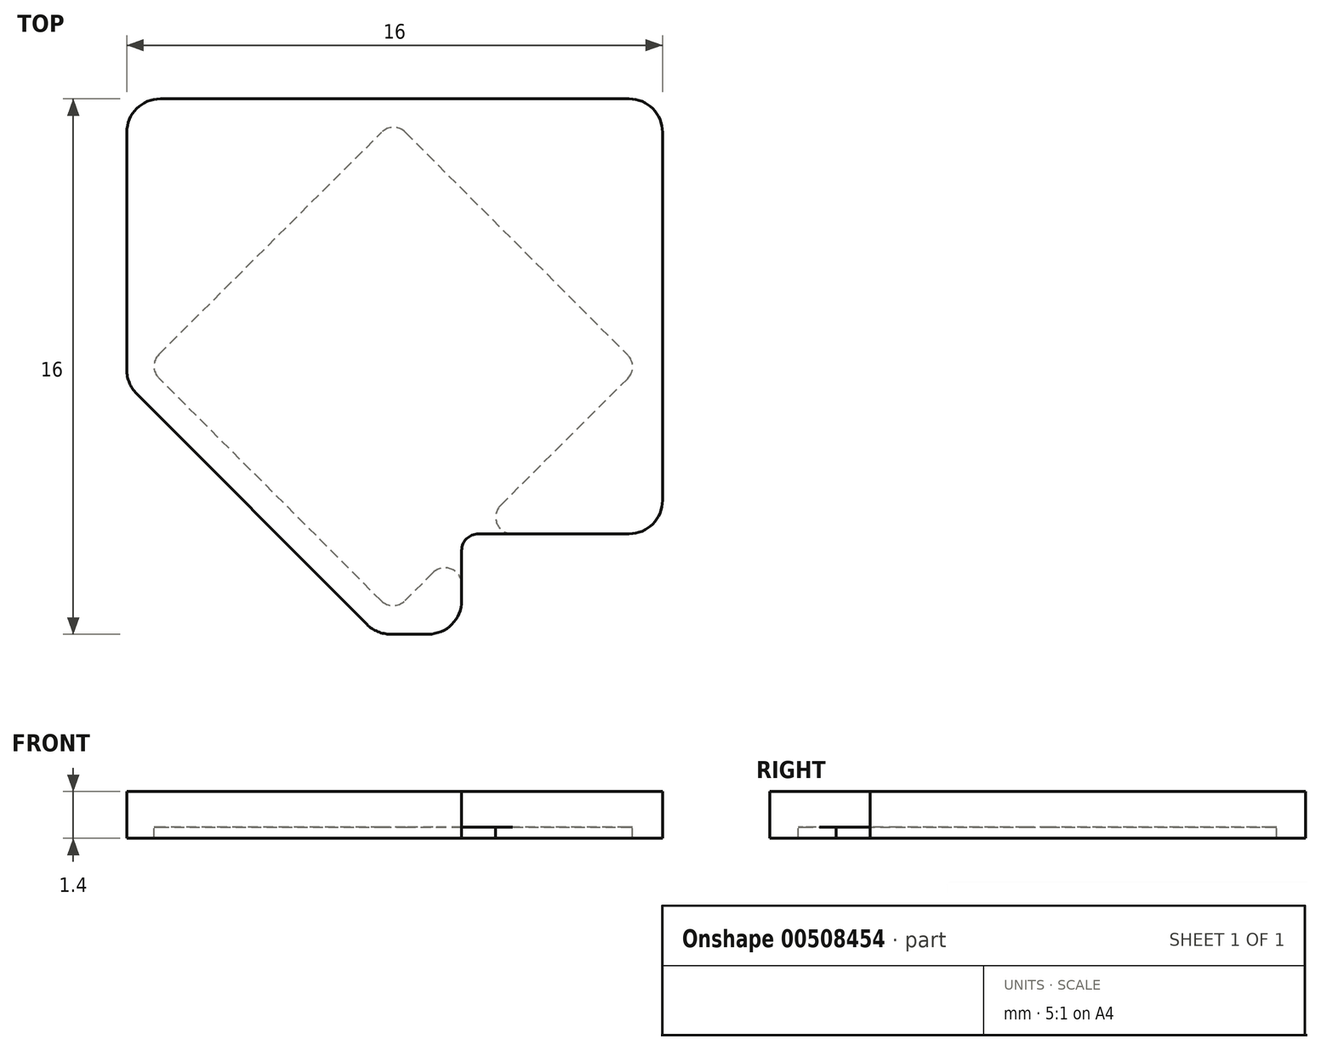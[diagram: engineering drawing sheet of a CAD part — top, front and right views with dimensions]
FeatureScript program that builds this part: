
annotation { "Feature Type Name" : "Feature", "Feature Type Description" : "" }
export const myFeature = defineFeature(function(context is Context, id is Id, definition is map)
    precondition{}
    {
        {
            var Q0;
            Q0=qCreatedBy(makeId("Top.planeOp"),FACE);
            var sketch = newSketch(context, id + "F0", { "sketchPlane" : qUnion([Q0])});
            skLineSegment(sketch, "E0.bottom", {"start": v(0, 0) * mm, "end": v(16, 0) * mm});
            skLineSegment(sketch, "E0.top", {"start": v(0, 16) * mm, "end": v(16, 16) * mm});
            skLineSegment(sketch, "E0.left", {"start": v(0, 0) * mm, "end": v(0, 16) * mm});
            skLineSegment(sketch, "E0.right", {"start": v(16, 0) * mm, "end": v(16, 16) * mm});
            skPoint(sketch, "E1.cCircle.centerSnap0", {"position": v(16, 8) * mm});
            skCircle(sketch, "E2.cCircle", {"center": v(7.96, 8) * mm, "radius": 5.2 * mm, "construction": true});
            skLineSegment(sketch, "E2.0", {"start": v(15.31, 8) * mm, "end": v(7.95, 0.65) * mm});
            skLineSegment(sketch, "E2.1", {"start": v(7.95, 0.65) * mm, "end": v(0.6, 8) * mm});
            skLineSegment(sketch, "E2.2", {"start": v(0.6, 8) * mm, "end": v(7.97, 15.35) * mm});
            skLineSegment(sketch, "E2.3", {"start": v(7.97, 15.35) * mm, "end": v(15.31, 8) * mm});
            skPoint(sketch, "E2.0.midPoint", {"position": v(11.63, 4.32) * mm});
            skLineSegment(sketch, "E3.bottom", {"start": v(16, 3) * mm, "end": v(10, 3) * mm});
            skLineSegment(sketch, "E3.top", {"start": v(16, 0) * mm, "end": v(10, 0) * mm});
            skLineSegment(sketch, "E3.left", {"start": v(16, 3) * mm, "end": v(16, 0) * mm});
            skLineSegment(sketch, "E3.right", {"start": v(10, 3) * mm, "end": v(10, 0) * mm});
            skLineSegment(sketch, "E4", {"start": v(2.16, 5.32) * mm, "end": v(5.62, 1.85) * mm});
            skLineSegment(sketch, "E5", {"start": v(2.16, 5.32) * mm, "end": v(0, 7.48) * mm});
            skLineSegment(sketch, "E6", {"start": v(5.62, 1.85) * mm, "end": v(7.46, 0) * mm});
            skSolve(sketch);
        }
        {
            var Q0;
            {var subQ11=sQuery(id+"F0.wireOp",EDGE,"E0.top");Q0=makeQuery(id+"F0.imprint","IMPRINT",FACE,{"disambiguationData":[TD([[makeQuery(id+"F0.imprint","IMPRINT",EDGE,{"derivedFrom":subQ11}),-1.0]])]});}
            extrude(context, id + "F1", {"entities" : qUnion([Q0]), "depth" : 1.4 * mm, "offsetDistance" : 25 * mm});
        }
        {
            var Q0;
            Q0=makeQuery(id+"F0.imprint","IMPRINT",FACE,{"disambiguationData":[TD([[makeQuery(id+"F0.imprint","IMPRINT",EDGE,{"derivedFrom":sQuery(id+"F0.wireOp",EDGE,"E2.0")}),-1.0]])]});
            extrude(context, id + "F2", {"entities" : qUnion([Q0]), "operationType" : NewBodyOperationType.ADD, "depth" : 1.4 * mm, "offsetDistance" : 25 * mm, "hasSecondDirection" : true, "secondDirectionOppositeDirection" : false, "secondDirectionDepth" : 0.33 * mm});
        }
        {
            var Q0;
            Q0=makeQuery(id+"F1.opExtrude","SWEPT_EDGE",EDGE,{"disambiguationData":[OSD([sQuery(id+"F0.wireOp",EDGE,"E0.bottom"),sQuery(id+"F0.wireOp",EDGE,"E0.left")])]});
            var Q1;
            Q1=makeQuery(id+"F1.opExtrude","SWEPT_EDGE",EDGE,{"disambiguationData":[OSD([sQuery(id+"F0.wireOp",EDGE,"E0.bottom"),sQuery(id+"F0.wireOp",EDGE,"E0.right")])]});
            var Q2;
            Q2=makeQuery(id+"F1.opExtrude","SWEPT_EDGE",EDGE,{"disambiguationData":[OSD([sQuery(id+"F0.wireOp",EDGE,"E0.top"),sQuery(id+"F0.wireOp",EDGE,"E0.right")])]});
            var Q3;
            Q3=makeQuery(id+"F1.opExtrude","SWEPT_EDGE",EDGE,{"disambiguationData":[OSD([sQuery(id+"F0.wireOp",EDGE,"E0.top"),sQuery(id+"F0.wireOp",EDGE,"E0.left")])]});
            var Q4;
            Q4=makeQuery(id+"F1.opExtrude","SWEPT_EDGE",EDGE,{"disambiguationData":[OSD([sQuery(id+"F0.wireOp",EDGE,"E0.bottom"),sQuery(id+"F0.wireOp",EDGE,"E3.top"),sQuery(id+"F0.wireOp",EDGE,"E3.right")])]});
            var Q5;
            Q5=makeQuery(id+"F1.opExtrude","SWEPT_EDGE",EDGE,{"disambiguationData":[OSD([sQuery(id+"F0.wireOp",EDGE,"E0.right"),sQuery(id+"F0.wireOp",EDGE,"E3.bottom"),sQuery(id+"F0.wireOp",EDGE,"E3.left")])]});
            fillet(context, id + "F3", {"entities" : qUnion([Q0, Q1, Q2, Q3, Q4, Q5]), "radius" : 1 * mm, "tangentPropagation" : true, "allowEdgeOverflow" : false});
        }
        {
            var Q0;
            Q0=makeQuery(id+"F1.opExtrude","SWEPT_EDGE",EDGE,{"disambiguationData":[OSD([sQuery(id+"F0.wireOp",EDGE,"E2.2"),sQuery(id+"F0.wireOp",EDGE,"E2.3")])]});
            var Q1;
            Q1=makeQuery(id+"F1.opExtrude","SWEPT_EDGE",EDGE,{"disambiguationData":[OSD([sQuery(id+"F0.wireOp",EDGE,"E2.1"),sQuery(id+"F0.wireOp",EDGE,"E2.2")])]});
            var Q2;
            Q2=makeQuery(id+"F1.opExtrude","SWEPT_EDGE",EDGE,{"disambiguationData":[OSD([sQuery(id+"F0.wireOp",EDGE,"E2.0"),sQuery(id+"F0.wireOp",EDGE,"E2.1")])]});
            var Q3;
            Q3=makeQuery(id+"F1.opExtrude","SWEPT_EDGE",EDGE,{"disambiguationData":[OSD([sQuery(id+"F0.wireOp",EDGE,"E2.0"),sQuery(id+"F0.wireOp",EDGE,"E2.3")])]});
            var Q4;
            Q4=makeQuery(id+"F1.opExtrude","SWEPT_EDGE",EDGE,{"disambiguationData":[OSD([sQuery(id+"F0.wireOp",EDGE,"E3.bottom"),sQuery(id+"F0.wireOp",EDGE,"E3.right")])]});
            var Q5;
            Q5=makeQuery(id+"F1.opExtrude","SWEPT_EDGE",EDGE,{"disambiguationData":[OSD([sQuery(id+"F0.wireOp",EDGE,"iXKTcPMj-XjcN-NIoc-TEQk-uKjJ4JOZThAX"),sQuery(id+"F0.wireOp",EDGE,"pTIPE4JI-hY1U-AWln-7atd-ccKZC95Nb6Ye")])]});
            var Q6;
            Q6=makeQuery(id+"F1.opExtrude","SWEPT_EDGE",EDGE,{"disambiguationData":[OSD([sQuery(id+"F0.wireOp",EDGE,"E4"),sQuery(id+"F0.wireOp",EDGE,"mLIsV41C-TQyn-wk8G-8JlF-niYuk90rkfJZ")])]});
            var Q7;
            Q7=makeQuery(id+"F1.opExtrude","SWEPT_EDGE",EDGE,{"disambiguationData":[OSD([sQuery(id+"F0.wireOp",EDGE,"pTIPE4JI-hY1U-AWln-7atd-ccKZC95Nb6Ye"),sQuery(id+"F0.wireOp",EDGE,"mLIsV41C-TQyn-wk8G-8JlF-niYuk90rkfJZ")])]});
            var Q8;
            Q8=makeQuery(id+"F1.opExtrude","SWEPT_EDGE",EDGE,{"disambiguationData":[OSD([sQuery(id+"F0.wireOp",EDGE,"E4"),sQuery(id+"F0.wireOp",EDGE,"iXKTcPMj-XjcN-NIoc-TEQk-uKjJ4JOZThAX")])]});
            fillet(context, id + "F4", {"entities" : qUnion([Q0, Q1, Q2, Q3, Q4, Q5, Q6, Q7, Q8]), "radius" : .5 * mm, "tangentPropagation" : true, "allowEdgeOverflow" : false});
        }
        {
            var Q0;
            Q0=makeQuery(id+"F2.opExtrude","SWEPT_EDGE",EDGE,{"disambiguationData":[OSD([sQuery(id+"F0.wireOp",EDGE,"E3.bottom"),sQuery(id+"F0.wireOp",EDGE,"E3.right")])]});
            fillet(context, id + "F5", {"entities" : qUnion([Q0]), "radius" : .5 * mm, "tangentPropagation" : true, "allowEdgeOverflow" : false});
        }
    });
